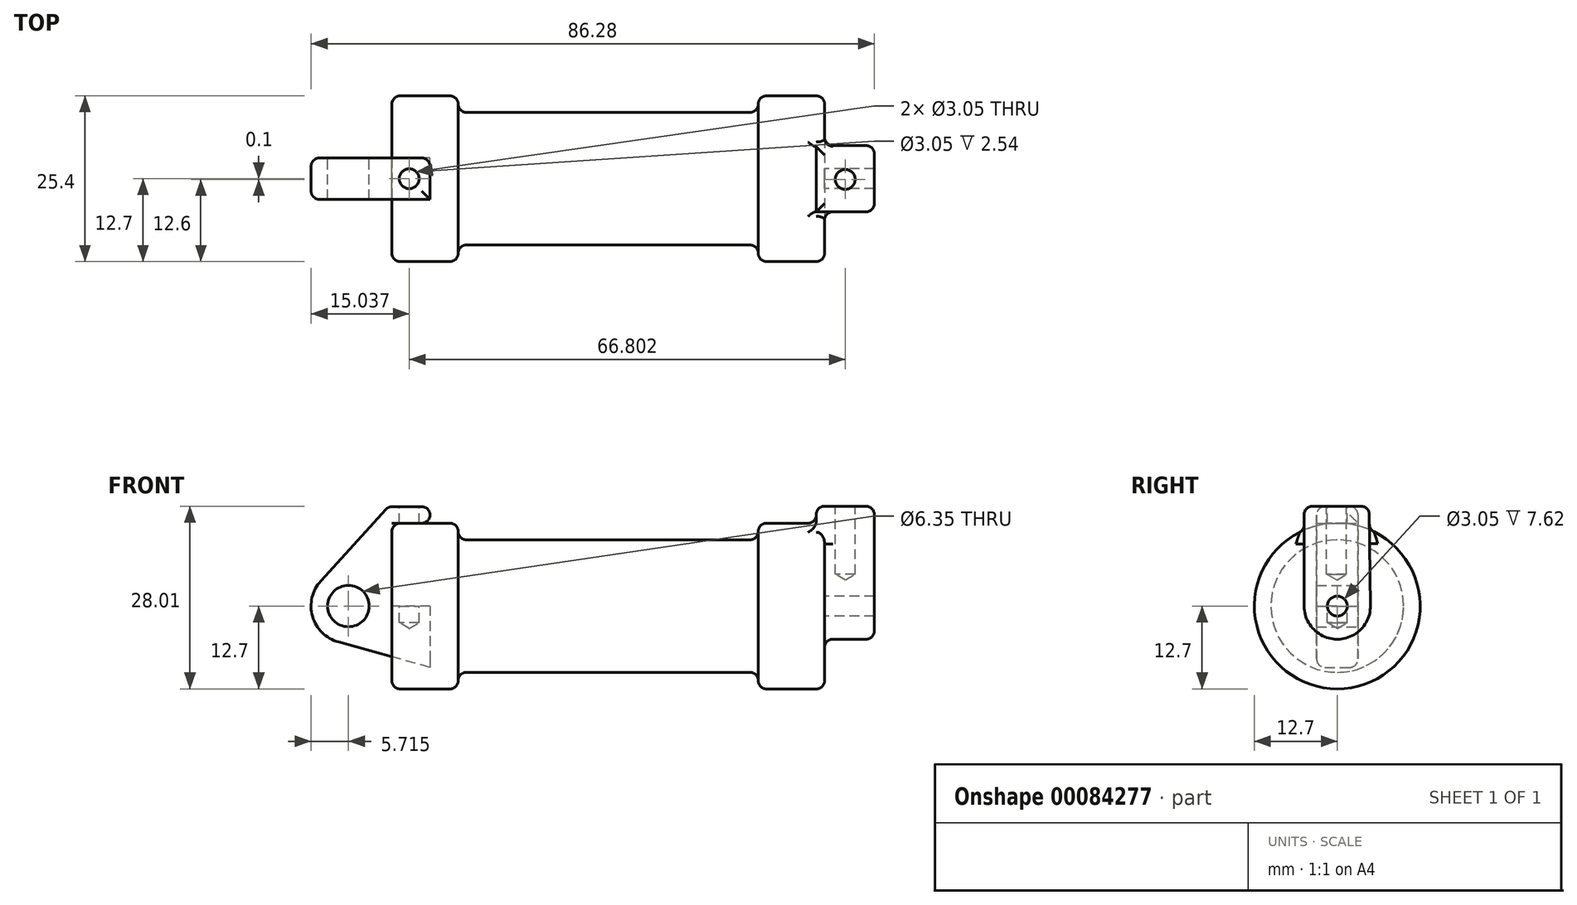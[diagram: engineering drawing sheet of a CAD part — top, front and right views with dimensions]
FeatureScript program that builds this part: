
annotation { "Feature Type Name" : "Feature", "Feature Type Description" : "" }
export const myFeature = defineFeature(function(context is Context, id is Id, definition is map)
    precondition{}
    {
        {
            var Q0;
            Q0=qCreatedBy(makeId("Front.planeOp"),FACE);
            var sketch = newSketch(context, id + "F0", { "sketchPlane" : qUnion([Q0])});
            skLineSegment(sketch, "E0", {"start": v(0, 0) * mm, "end": v(0, 12.7) * mm});
            skLineSegment(sketch, "E1", {"start": v(0, 12.7) * mm, "end": v(10.16, 12.7) * mm});
            skLineSegment(sketch, "E2", {"start": v(10.16, 12.7) * mm, "end": v(10.16, 10.16) * mm});
            skLineSegment(sketch, "E3", {"start": v(10.16, 10.16) * mm, "end": v(56.13, 10.16) * mm});
            skLineSegment(sketch, "E4", {"start": v(56.13, 10.16) * mm, "end": v(56.13, 12.7) * mm});
            skLineSegment(sketch, "E5", {"start": v(56.13, 12.7) * mm, "end": v(66.3, 12.7) * mm});
            skLineSegment(sketch, "E6", {"start": v(66.3, 12.7) * mm, "end": v(66.3, 0) * mm});
            skLineSegment(sketch, "E7", {"start": v(66.3, 0) * mm, "end": v(0, 0) * mm});
            skLineSegment(sketch, "E8", {"start": v(5.84, 15.24) * mm, "end": v(-0.5, 15.24) * mm});
            skLineSegment(sketch, "E9", {"start": v(-0.5, 15.24) * mm, "end": v(-10.88, 3.85) * mm});
            skLineSegment(sketch, "E10", {"start": v(0, 0) * mm, "end": v(-6.65, 0) * mm});
            skCircle(sketch, "E11", {"center": v(-6.65, 0) * mm, "radius": 5.72 * mm});
            skCircle(sketch, "E12", {"center": v(-6.65, 0) * mm, "radius": 3.18 * mm});
            skLineSegment(sketch, "E13", {"start": v(5.84, 15.24) * mm, "end": v(5.84, -9.4) * mm});
            skLineSegment(sketch, "E14", {"start": v(5.84, -9.4) * mm, "end": v(-8.18, -5.5) * mm});
            skSolve(sketch);
        }
        {
            var Q0;
            {var subQ0=sQuery(id+"F0.wireOp",EDGE,"E0");Q0=makeQuery(id+"F0.imprint","IMPRINT",FACE,{"disambiguationData":[TD([[makeQuery(id+"F0.imprint","IMPRINT",EDGE,{"derivedFrom":subQ0}),-1.0]])]});}
            var Q1;
            {var subQ0=sQuery(id+"F0.wireOp",EDGE,"E2");Q1=makeQuery(id+"F0.imprint","IMPRINT",FACE,{"disambiguationData":[TD([[makeQuery(id+"F0.imprint","IMPRINT",EDGE,{"derivedFrom":subQ0}),-1.0]])]});}
            var Q2;
            Q2=sQuery(id+"F0.wireOp",EDGE,"E7");
            revolve(context, id + "F1", {"entities" : qUnion([Q0, Q1]), "axis" : qUnion([Q2]), "revolveType" : RevolveType.FULL});
        }
        {
            var Q0;
            {var subQ3=sQuery(id+"F0.wireOp",EDGE,"E0");Q0=makeQuery(id+"F0.imprint","IMPRINT",FACE,{"disambiguationData":[TD([[makeQuery(id+"F0.imprint","IMPRINT",EDGE,{"derivedFrom":subQ3}),1.0]])]});}
            var Q1;
            {var subQ0=sQuery(id+"F0.wireOp",EDGE,"E14");Q1=makeQuery(id+"F0.imprint","IMPRINT",FACE,{"disambiguationData":[TD([[makeQuery(id+"F0.imprint","IMPRINT",EDGE,{"derivedFrom":subQ0}),-1.0]])]});}
            var Q2;
            {var subQ4=sQuery(id+"F0.wireOp",EDGE,"E12");Q2=makeQuery(id+"F0.imprint","IMPRINT",FACE,{"disambiguationData":[TD([[makeQuery(id+"F0.imprint","IMPRINT",EDGE,{"derivedFrom":subQ4}),-1.0]])]});}
            extrude(context, id + "F2", {"entities" : qUnion([Q0, Q1, Q2]), "endBound" : BoundingType.SYMMETRIC, "depth" : 6.35 * mm});
        }
        {
            var Q0;
            Q0=makeQuery(id+"F1.opRevolve","SWEPT_FACE",FACE,{"disambiguationData":[OSD([sQuery(id+"F0.wireOp",EDGE,"E6")])]});
            var sketch = newSketch(context, id + "F3", { "sketchPlane" : qUnion([Q0])});
            skCircle(sketch, "E15", {"center": v(0, 0) * mm, "radius": 5.08 * mm});
            skCircle(sketch, "E16", {"center": v(0, 0) * mm, "radius": 1.52 * mm});
            skLineSegment(sketch, "E17", {"start": v(-5.08, 0) * mm, "end": v(-5.08, 15.3) * mm});
            skLineSegment(sketch, "E18", {"start": v(-5.08, 15.3) * mm, "end": v(4.88, 15.3) * mm});
            skLineSegment(sketch, "E19", {"start": v(4.88, 15.3) * mm, "end": v(5.08, 0.07) * mm});
            skSolve(sketch);
        }
        {
            var Q0;
            Q0 = qSketchRegion(id + "F3", true);
            extrude(context, id + "F4", {"entities" : qUnion([Q0]), "operationType" : NewBodyOperationType.ADD, "depth" : 7.62 * mm, "hasSecondDirection" : true, "secondDirectionOppositeDirection" : true, "secondDirectionDepth" : 1.27 * mm});
        }
        {
            var Q0;
            Q0=makeQuery(id+"F2.opExtrude","SWEPT_FACE",FACE,{"disambiguationData":[OSD([sQuery(id+"F0.wireOp",EDGE,"E8")])]});
            var sketch = newSketch(context, id + "F5", { "sketchPlane" : qUnion([Q0])});
            skLineSegment(sketch, "E20", {"start": v(-0.5, 3.18) * mm, "end": v(5.84, -3.18) * mm, "construction": true});
            skLineSegment(sketch, "E21", {"start": v(-0.5, -3.18) * mm, "end": v(5.84, 3.18) * mm, "construction": true});
            skCircle(sketch, "E22", {"center": v(2.67, 0) * mm, "radius": 1.05 * mm});
            skSolve(sketch);
        }
        {
            var Q0;
            Q0=sQuery(id+"F5.wireOp",VERTEX,"E22.center");
            var Q1;
            Q1=makeQuery(id+"F2.opExtrude","SWEPT_BODY",BODY,{"disambiguationData":[OSD([sQuery(id+"F0.wireOp",EDGE,"E0"),sQuery(id+"F0.wireOp",EDGE,"E1"),sQuery(id+"F0.wireOp",EDGE,"E7"),sQuery(id+"F0.wireOp",EDGE,"E8"),sQuery(id+"F0.wireOp",EDGE,"E9"),sQuery(id+"F0.wireOp",EDGE,"E11"),sQuery(id+"F0.wireOp",EDGE,"E12"),sQuery(id+"F0.wireOp",EDGE,"E13"),sQuery(id+"F0.wireOp",EDGE,"E14")])]});
            hole(context, id + "F6", {"style" : HoleStyle.SIMPLE, "endStyle" : HoleEndStyle.BLIND, "holeDiameter" : 3.05 * mm, "holeDepth" : 17.78 * mm, "locations" : qUnion([Q0]), "scope" : qUnion([Q1])});
        }
        {
            var Q0;
            Q0=makeQuery(id+"F4.opExtrude","SWEPT_FACE",FACE,{"disambiguationData":[OSD([sQuery(id+"F3.wireOp",EDGE,"E18")])]});
            var sketch = newSketch(context, id + "F7", { "sketchPlane" : qUnion([Q0])});
            skLineSegment(sketch, "E23", {"start": v(65.02, 4.88) * mm, "end": v(73.91, -5.08) * mm, "construction": true});
            skLineSegment(sketch, "E24", {"start": v(65.02, -5.08) * mm, "end": v(73.91, 4.88) * mm, "construction": true});
            skCircle(sketch, "E25", {"center": v(69.47, -0.1) * mm, "radius": 1.61 * mm, "construction": true});
            skSolve(sketch);
        }
        {
            var Q0;
            Q0=sQuery(id+"F7.wireOp",VERTEX,"E25.center");
            var Q1;
            Q1=makeQuery(id+"F1.opRevolve","SWEPT_BODY",BODY,{"disambiguationData":[OSD([sQuery(id+"F0.wireOp",EDGE,"E0"),sQuery(id+"F0.wireOp",EDGE,"E1"),sQuery(id+"F0.wireOp",EDGE,"E2"),sQuery(id+"F0.wireOp",EDGE,"E3"),sQuery(id+"F0.wireOp",EDGE,"E4"),sQuery(id+"F0.wireOp",EDGE,"E5"),sQuery(id+"F0.wireOp",EDGE,"E6"),sQuery(id+"F0.wireOp",EDGE,"E7")])]});
            hole(context, id + "F8", {"style" : HoleStyle.SIMPLE, "endStyle" : HoleEndStyle.BLIND, "holeDiameter" : 3.05 * mm, "holeDepth" : 10.4 * mm, "locations" : qUnion([Q0]), "scope" : qUnion([Q1])});
        }
        {
            var Q0;
            Q0=makeQuery(id+"F1.opRevolve","SWEPT_EDGE",EDGE,{"disambiguationData":[OSD([sQuery(id+"F0.wireOp",EDGE,"E1"),sQuery(id+"F0.wireOp",EDGE,"E2")])]});
            var Q1;
            Q1=makeQuery(id+"F1.opRevolve","SWEPT_EDGE",EDGE,{"disambiguationData":[OSD([sQuery(id+"F0.wireOp",EDGE,"E4"),sQuery(id+"F0.wireOp",EDGE,"E5")])]});
            var Q2;
            Q2=makeQuery(id+"F1.opRevolve","SWEPT_EDGE",EDGE,{"disambiguationData":[OSD([sQuery(id+"F0.wireOp",EDGE,"E3"),sQuery(id+"F0.wireOp",EDGE,"E4")])]});
            var Q3;
            Q3=makeQuery(id+"F1.opRevolve","SWEPT_EDGE",EDGE,{"disambiguationData":[OSD([sQuery(id+"F0.wireOp",EDGE,"E2"),sQuery(id+"F0.wireOp",EDGE,"E3")])]});
            var Q4;
            Q4=makeQuery(id+"F1.opRevolve","SWEPT_EDGE",EDGE,{"disambiguationData":[OSD([sQuery(id+"F0.wireOp",EDGE,"E5"),sQuery(id+"F0.wireOp",EDGE,"E6")])]});
            var Q5;
            Q5=makeQuery(id+"F1.opRevolve","SWEPT_EDGE",EDGE,{"disambiguationData":[OSD([sQuery(id+"F0.wireOp",EDGE,"E0"),sQuery(id+"F0.wireOp",EDGE,"E1")])]});
            fillet(context, id + "F9", {"entities" : qUnion([Q0, Q1, Q2, Q3, Q4, Q5]), "radius" : 1.27 * mm, "tangentPropagation" : true, "allowEdgeOverflow" : false});
        }
        {
            var Q0;
            Q0=makeQuery(id+"F4.opExtrude","CAP_EDGE",EDGE,{"disambiguationData":[OSD([sQuery(id+"F3.wireOp",EDGE,"E17")])],"isStart":false});
            var Q1;
            Q1=makeQuery(id+"F4.opExtrude","CAP_EDGE",EDGE,{"disambiguationData":[OSD([sQuery(id+"F3.wireOp",EDGE,"E19")])],"isStart":false});
            var Q2;
            Q2=makeQuery(id+"F4.boolean.opBoolean","INTERSECT",EDGE,{"derivedFrom":[makeQuery(id+"F1.opRevolve","SWEPT_FACE",FACE,{"disambiguationData":[OSD([sQuery(id+"F0.wireOp",EDGE,"E6")])]}),makeQuery(id+"F4.opExtrude","SWEPT_FACE",FACE,{"disambiguationData":[OSD([sQuery(id+"F3.wireOp",EDGE,"E17")])]})]});
            var Q3;
            Q3=makeQuery(id+"F4.opExtrude","SWEPT_EDGE",EDGE,{"disambiguationData":[OSD([sQuery(id+"F3.wireOp",EDGE,"E17"),sQuery(id+"F3.wireOp",EDGE,"E18")])]});
            var Q4;
            Q4=makeQuery(id+"F4.opExtrude","CAP_EDGE",EDGE,{"disambiguationData":[OSD([sQuery(id+"F3.wireOp",EDGE,"E18")])],"isStart":false});
            var Q5;
            Q5=makeQuery(id+"F4.opExtrude","SWEPT_EDGE",EDGE,{"disambiguationData":[OSD([sQuery(id+"F3.wireOp",EDGE,"E18"),sQuery(id+"F3.wireOp",EDGE,"E19")])]});
            var Q6;
            Q6=makeQuery(id+"F4.boolean.opBoolean","INTERSECT",EDGE,{"derivedFrom":[makeQuery(id+"F1.opRevolve","SWEPT_FACE",FACE,{"disambiguationData":[OSD([sQuery(id+"F0.wireOp",EDGE,"E5")])]}),makeQuery(id+"F4.opExtrude","CAP_FACE",FACE,{"disambiguationData":[OSD([sQuery(id+"F3.wireOp",EDGE,"E15"),sQuery(id+"F3.wireOp",EDGE,"E16"),sQuery(id+"F3.wireOp",EDGE,"E17"),sQuery(id+"F3.wireOp",EDGE,"E18"),sQuery(id+"F3.wireOp",EDGE,"E19")])],"isStart":true})]});
            var Q7;
            Q7=makeQuery(id+"F4.opExtrude","CAP_EDGE",EDGE,{"disambiguationData":[OSD([sQuery(id+"F3.wireOp",EDGE,"E18")])],"isStart":true});
            fillet(context, id + "F10", {"entities" : qUnion([Q0, Q1, Q2, Q3, Q4, Q5, Q6, Q7]), "radius" : 1.27 * mm, "tangentPropagation" : true, "allowEdgeOverflow" : false});
        }
        {
            var Q0;
            Q0=makeQuery(id+"F2.opExtrude","CAP_EDGE",EDGE,{"disambiguationData":[OSD([sQuery(id+"F0.wireOp",EDGE,"E9")])],"isStart":true});
            var Q1;
            Q1=makeQuery(id+"F2.opExtrude","CAP_EDGE",EDGE,{"disambiguationData":[OSD([sQuery(id+"F0.wireOp",EDGE,"E8")])],"isStart":true});
            var Q2;
            {var subQ0=sQuery(id+"F0.wireOp",EDGE,"E13");Q2=makeQuery(id+"F2.opExtrude","CAP_EDGE",EDGE,{"disambiguationData":[OSD([subQ0]),TDD([makeQuery(id+"F0.imprint","IMPRINT",EDGE,{"disambiguationData":[TD([[makeQuery(id+"F0.imprint","INTERSECT",VERTEX,{"derivedFrom":[sQuery(id+"F0.wireOp",EDGE,"E8"),subQ0]}),-1.0]])],"derivedFrom":subQ0})])],"isStart":true});}
            var Q3;
            Q3=makeQuery(id+"F2.opExtrude","CAP_EDGE",EDGE,{"disambiguationData":[OSD([sQuery(id+"F0.wireOp",EDGE,"E9")])],"isStart":false});
            var Q4;
            Q4=makeQuery(id+"F2.opExtrude","SWEPT_EDGE",EDGE,{"disambiguationData":[OSD([sQuery(id+"F0.wireOp",EDGE,"E8"),sQuery(id+"F0.wireOp",EDGE,"E9")])]});
            var Q5;
            Q5=makeQuery(id+"F2.opExtrude","CAP_EDGE",EDGE,{"disambiguationData":[OSD([sQuery(id+"F0.wireOp",EDGE,"E8")])],"isStart":false});
            var Q6;
            Q6=makeQuery(id+"F2.opExtrude","SWEPT_EDGE",EDGE,{"disambiguationData":[OSD([sQuery(id+"F0.wireOp",EDGE,"E8"),sQuery(id+"F0.wireOp",EDGE,"E13")])]});
            var Q7;
            Q7=makeQuery(id+"F2.opExtrude","SWEPT_EDGE",EDGE,{"disambiguationData":[OSD([sQuery(id+"F0.wireOp",EDGE,"E1"),sQuery(id+"F0.wireOp",EDGE,"E13")])]});
            fillet(context, id + "F11", {"entities" : qUnion([Q0, Q1, Q2, Q3, Q4, Q5, Q6, Q7]), "radius" : 1.27 * mm, "tangentPropagation" : true, "allowEdgeOverflow" : false});
        }
    });
